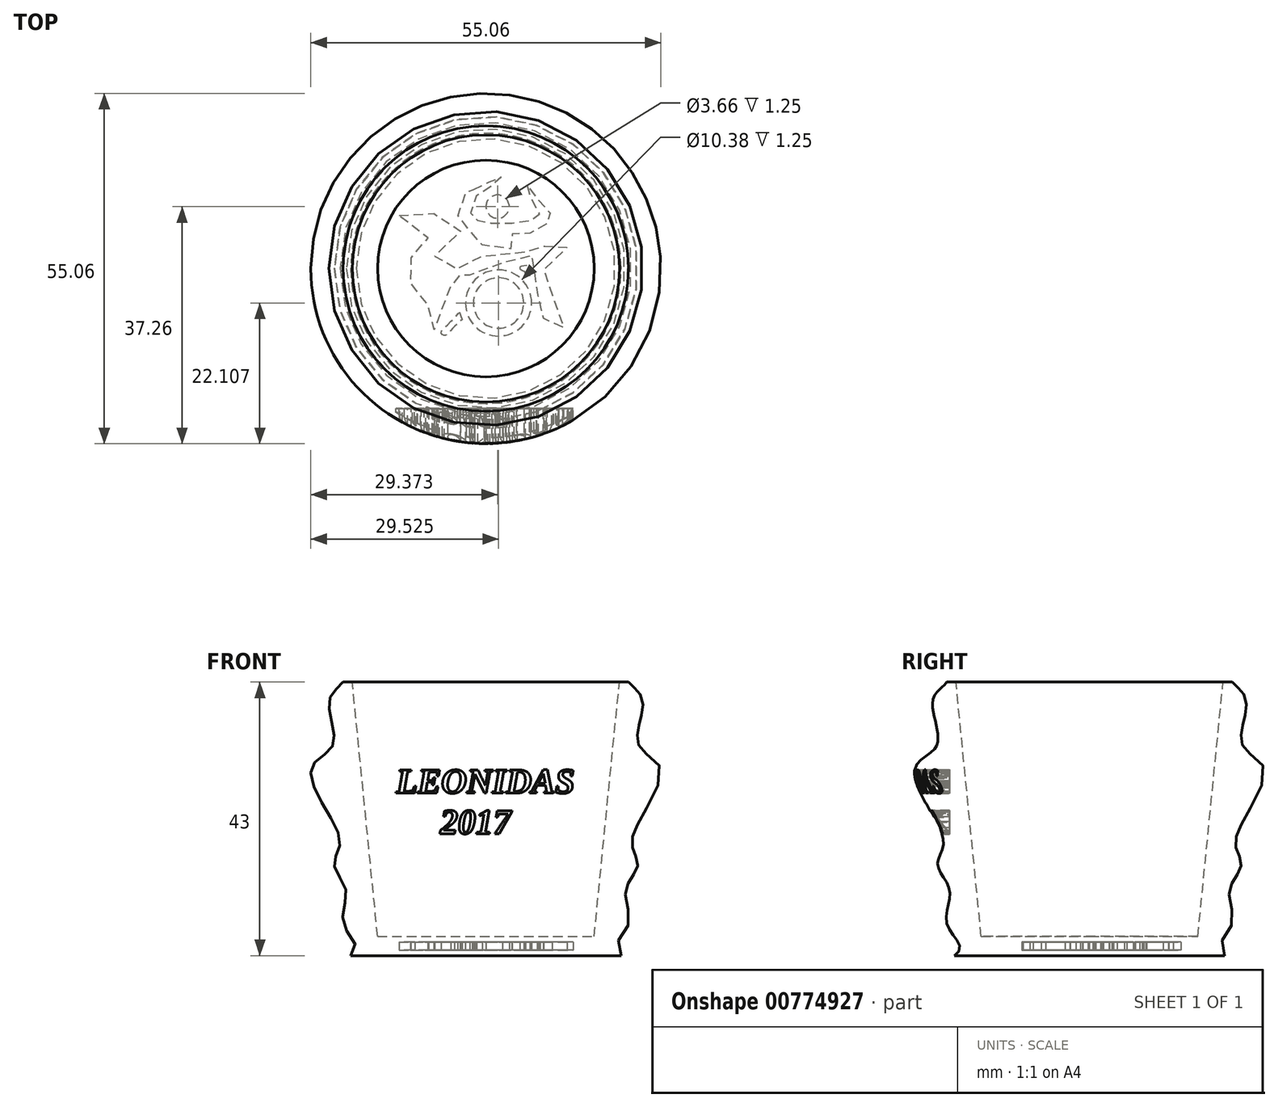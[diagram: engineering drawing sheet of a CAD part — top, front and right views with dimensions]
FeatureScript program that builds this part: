
annotation { "Feature Type Name" : "Feature", "Feature Type Description" : "" }
export const myFeature = defineFeature(function(context is Context, id is Id, definition is map)
    precondition{}
    {
        {
            var Q0;
            Q0=qCreatedBy(makeId("Front.planeOp"),FACE);
            var sketch = newSketch(context, id + "F0", { "sketchPlane" : qUnion([Q0])});
            skLineSegment(sketch, "E0", {"start": v(22.45, 43) * mm, "end": v(21, 43) * mm});
            skLineSegment(sketch, "E1", {"start": v(21, 43) * mm, "end": v(17.03, 3) * mm});
            skLineSegment(sketch, "E2", {"start": v(17.03, 3) * mm, "end": v(0, 3) * mm});
            skLineSegment(sketch, "E3", {"start": v(15.16, 0) * mm, "end": v(0, 0) * mm});
            skLineSegment(sketch, "E4", {"start": v(0, 0) * mm, "end": v(0, 3) * mm});
            skLineSegment(sketch, "E5", {"start": v(15.16, 0) * mm, "end": v(21.26, 0) * mm});
            skFitSpline(sketch, "E6", {"points": [v(21.26, 0) * mm, v(22.3, 4.61) * mm, v(21.97, 10.14) * mm, v(23.88, 14.27) * mm, v(22.95, 17.55) * mm, v(25.87, 24.2) * mm, v(27.28, 29.9) * mm, v(24.26, 32.61) * mm, v(24.2, 36.65) * mm, v(24.41, 40.88) * mm, v(22.45, 43) * mm], "startDerivative": vector(-64.03, 39.45) * mm, "endDerivative": vector(-12.25, 23.77) * mm});
            skSolve(sketch);
        }
        {
            var Q0;
            Q0=qSketchRegion(id+"F0",true);
            var Q1;
            Q1=sQuery(id+"F0.wireOp",EDGE,"E4");
            revolve(context, id + "F1", {"surfaceOperationType" : NewSurfaceOperationType.NEW, "entities" : qUnion([Q0]), "axis" : qUnion([Q1]), "revolveType" : RevolveType.FULL});
        }
        {
            var Q0;
            Q0=qCreatedBy(makeId("Top.planeOp"),FACE);
            cPlane(context, id + "F2", {"entities" : qUnion([Q0]), "cplaneType" : CPlaneType.OFFSET, "offset" : 1.5 * mm, "width" : 150 * mm, "height" : 150 * mm});
        }
        {
            var Q0;
            Q0=qCreatedBy(id+"F2.planeOp",FACE);
            var sketch = newSketch(context, id + "F3", { "sketchPlane" : qUnion([Q0])});
            skFitSpline(sketch, "E7", {"points": [v(-13.66, 8.35) * mm, v(-12.15, 8.52) * mm, v(-10.61, 8.5) * mm, v(-9.42, 8.3) * mm, v(-9.1, 8.32) * mm, v(-9.04, 8.6) * mm, v(-8.61, 8.95) * mm, v(-8.2, 8.66) * mm, v(-8.13, 8.12) * mm, v(-8.1, 8.01) * mm, v(-7.15, 7.7) * mm, v(-6.07, 7.27) * mm, v(-5.15, 6.75) * mm, v(-3.96, 6.08) * mm, v(-3.83, 5.9) * mm, v(-4.16, 5.9) * mm, v(-6.38, 6.46) * mm, v(-7.96, 6.86) * mm, v(-8.05, 6.86) * mm, v(-8.07, 6.46) * mm, v(-8.07, 1.94) * mm, v(-8.02, 1.9) * mm, v(-5.5, 1.92) * mm, v(-5.06, 1.74) * mm, v(-5, 1.25) * mm, v(-5.33, 0.89) * mm, v(-5.49, 0.86) * mm, v(-5.48, 0) * mm, v(-5.33, -0.04) * mm, v(-1.8, -0.06) * mm, v(-1.68, -0.01) * mm, v(-1.68, 0.32) * mm, v(-1.7, 0.85) * mm, v(-1.78, 0.9) * mm, v(-2.1, 1.13) * mm, v(-2.07, 1.67) * mm, v(-1.53, 1.88) * mm, v(0.6, 1.9) * mm, v(3.43, 1.9) * mm, v(4.27, 1.87) * mm, v(4.51, 1.76) * mm, v(4.74, 1.8) * mm, v(5.28, 2.11) * mm, v(6.26, 2.68) * mm, v(7.72, 3.2) * mm, v(8.17, 3.34) * mm, v(8.12, 3.6) * mm, v(8.21, 4.06) * mm, v(8.57, 4.34) * mm, v(8.93, 4.2) * mm, v(9.08, 3.8) * mm, v(9.1, 3.5) * mm, v(9.25, 3.54) * mm, v(9.9, 3.7) * mm, v(11.26, 3.75) * mm, v(12.15, 3.77) * mm, v(12.97, 3.72) * mm, v(13.66, 3.7) * mm, v(13.66, 3.5) * mm, v(12.88, 3.32) * mm, v(11.78, 3.05) * mm, v(10.77, 2.8) * mm, v(10.15, 2.69) * mm, v(9.35, 2.48) * mm, v(9.08, 2.4) * mm, v(9.07, 2.13) * mm, v(9.09, -1.13) * mm, v(9.02, -5.98) * mm, v(9.12, -6.2) * mm, v(10.61, -7.63) * mm, v(12.01, -9.1) * mm, v(12.74, -9.9) * mm, v(12.74, -10.27) * mm, v(12.43, -10.43) * mm, v(12.17, -10.46) * mm, v(11.7, -10.05) * mm, v(9.34, -7.73) * mm, v(9.06, -7.6) * mm, v(9.12, -8.2) * mm, v(8.9, -8.78) * mm, v(8.32, -8.78) * mm, v(8.1, -8.05) * mm, v(8.13, -6.92) * mm, v(8.33, -5.31) * mm, v(8.22, -4.15) * mm, v(8.11, -3.63) * mm, v(8.1, -1.35) * mm, v(8.11, 0.64) * mm, v(8.13, 2.1) * mm, v(8.11, 2.2) * mm, v(7.38, 2.03) * mm, v(5.56, 1.55) * mm, v(4.7, 1.33) * mm, v(4.61, 1.19) * mm, v(4.48, 1) * mm, v(4.23, 0.92) * mm, v(4.14, 0.85) * mm, v(4.16, 0.64) * mm, v(4.15, 0.55) * mm, v(3.55, 0.78) * mm, v(1.83, 0.94) * mm, v(0.7, 0.8) * mm, v(-0.14, 0.59) * mm, v(-1.2, 0.08) * mm, v(-1.38, -0.08) * mm, v(-1.8, -0.42) * mm, v(-2.18, -0.65) * mm, v(-3.6, -2.3) * mm, v(-3.88, -3.14) * mm, v(-4.04, -3.83) * mm, v(-4.06, -2.77) * mm, v(-4.05, -1.84) * mm, v(-4.05, -1.14) * mm, v(-4.05, -1.1) * mm, v(-4.43, -1.1) * mm, v(-5.42, -1.09) * mm, v(-5.47, -1.18) * mm, v(-5.51, -1.68) * mm, v(-5.48, -2.1) * mm, v(-5.35, -2.12) * mm, v(-5.02, -2.33) * mm, v(-4.97, -2.74) * mm, v(-5.18, -2.98) * mm, v(-5.26, -3.03) * mm, v(-5.46, -3.04) * mm, v(-7.94, -3.01) * mm, v(-8.12, -3.07) * mm, v(-8.1, -3.52) * mm, v(-8.15, -7.66) * mm, v(-8.15, -9.17) * mm, v(-8.12, -10.17) * mm, v(-8.19, -10.33) * mm, v(-8.46, -10.52) * mm, v(-8.77, -10.5) * mm, v(-8.96, -10.3) * mm, v(-9.1, -10.03) * mm, v(-9.04, -8.29) * mm, v(-9.1, -5.76) * mm, v(-9.08, -3.88) * mm, v(-9.04, -3.2) * mm, v(-9.08, -3.04) * mm, v(-9.42, -3.07) * mm, v(-11.4, -3.03) * mm, v(-11.7, -2.9) * mm, v(-11.78, -2.55) * mm, v(-11.75, -2.29) * mm, v(-11.46, -2.15) * mm, v(-11.22, -2.02) * mm, v(-11.19, 0) * mm, v(-11.19, 0.63) * mm, v(-11.24, 0.89) * mm, v(-11.44, 0.93) * mm, v(-11.77, 1.16) * mm, v(-11.86, 1.5) * mm, v(-11.75, 1.69) * mm, v(-11.58, 1.83) * mm, v(-11.3, 1.9) * mm, v(-10.97, 1.93) * mm, v(-10.43, 1.92) * mm, v(-9.76, 1.91) * mm, v(-9.3, 1.9) * mm, v(-9.22, 1.9) * mm, v(-9.13, 1.9) * mm, v(-9.1, 2) * mm, v(-9.1, 5.64) * mm, v(-9.11, 6.43) * mm, v(-9.12, 7.02) * mm, v(-9.18, 7.15) * mm, v(-9.99, 7.33) * mm, v(-12.26, 7.85) * mm, v(-13.66, 8.35) * mm]});
            skFitSpline(sketch, "E8", {"points": [v(5.35, -0.07) * mm, v(5.6, -0.19) * mm, v(6.01, -0.5) * mm, v(6.41, -0.86) * mm, v(6.67, -1.13) * mm, v(6.92, -1.44) * mm, v(6.92, -1.35) * mm, v(6.91, -0.4) * mm, v(6.92, 0.34) * mm, v(6.9, 0.64) * mm, v(6.8, 0.6) * mm, v(6.23, 0.46) * mm, v(5.44, 0.29) * mm, v(5.36, 0.26) * mm, v(5.35, -0.07) * mm]});
            skFitSpline(sketch, "E9", {"points": [v(-4.1, -6.9) * mm, v(-4.03, -7.23) * mm, v(-3.87, -7.7) * mm, v(-3.72, -8) * mm, v(-3.98, -8.27) * mm, v(-4.83, -9.06) * mm, v(-5.58, -9.8) * mm, v(-6.24, -10.46) * mm, v(-6.6, -10.54) * mm, v(-6.92, -10.33) * mm, v(-7.02, -10.08) * mm, v(-6.92, -9.74) * mm, v(-6.6, -9.42) * mm, v(-5.37, -8.18) * mm, v(-4.59, -7.4) * mm, v(-4.1, -6.9) * mm]});
            skCircle(sketch, "E10", {"center": v(2, -5.42) * mm, "radius": 3.96 * mm});
            skCircle(sketch, "E11", {"center": v(2, -5.42) * mm, "radius": 5.2 * mm});
            skCircle(sketch, "E12", {"center": v(1.84, 9.73) * mm, "radius": 1.83 * mm});
            skFitSpline(sketch, "E13", {"points": [v(-1.95, 12.44) * mm, v(-1.18, 12.85) * mm, v(-0.4, 13.18) * mm, v(0.41, 13.53) * mm, v(0.86, 13.72) * mm, v(1.48, 13.96) * mm, v(1.87, 14.15) * mm, v(2.26, 14.3) * mm, v(2.41, 14.36) * mm, v(2.62, 14.22) * mm, v(2.57, 13.98) * mm, v(2.11, 13.66) * mm, v(1.13, 13.12) * mm, v(-1.1, 11.9) * mm, v(-1.4, 11.74) * mm, v(-1.47, 11.64) * mm, v(-1.46, 11.54) * mm, v(-1.57, 11.2) * mm, v(-2.08, 9.65) * mm, v(-2.27, 9.2) * mm, v(-2.4, 8.75) * mm, v(-2.52, 8.43) * mm, v(-2.52, 8.33) * mm, v(-2.27, 8.15) * mm, v(-1.8, 7.9) * mm, v(-1.38, 7.63) * mm, v(-1, 7.42) * mm, v(-0.7, 7.26) * mm, v(-0.57, 7.2) * mm, v(-0.35, 7.2) * mm, v(0.86, 7.15) * mm, v(1.6, 7.15) * mm, v(3.09, 7.15) * mm, v(4.84, 7.16) * mm, v(6.33, 7.18) * mm, v(6.44, 7.18) * mm, v(6.6, 7.27) * mm, v(7.52, 7.82) * mm, v(7.8, 7.97) * mm, v(8.11, 8.17) * mm, v(8.48, 8.38) * mm, v(8.54, 8.47) * mm, v(8.43, 8.61) * mm, v(7.96, 9.55) * mm, v(7.56, 10.3) * mm, v(6.72, 11.87) * mm, v(6.34, 12.6) * mm, v(6.28, 12.81) * mm, v(6.27, 13) * mm, v(6.35, 13.09) * mm, v(6.44, 13.13) * mm, v(6.56, 13.12) * mm, v(6.62, 13.07) * mm, v(6.73, 12.95) * mm, v(6.97, 12.59) * mm, v(8, 11.07) * mm, v(9.4, 8.9) * mm, v(9.44, 8.86) * mm, v(9.67, 8.88) * mm, v(9.97, 8.8) * mm, v(10.31, 8.48) * mm, v(10.44, 7.9) * mm, v(10.2, 7.45) * mm, v(9.81, 7.17) * mm, v(9.33, 6.9) * mm, v(7.35, 5.74) * mm, v(7.21, 5.65) * mm, v(7.01, 5.55) * mm, v(6.62, 5.51) * mm, v(5, 5.46) * mm, v(4.34, 5.46) * mm, v(4.17, 5.45) * mm, v(4.07, 5.35) * mm, v(4.08, 5.11) * mm, v(4.09, 3.35) * mm, v(4.06, 3.13) * mm, v(3.84, 3.1) * mm, v(-0.45, 3.1) * mm, v(-0.56, 3.1) * mm, v(-0.56, 5.1) * mm, v(-0.56, 5.18) * mm, v(-0.68, 5.25) * mm, v(-4, 7.24) * mm, v(-4.19, 7.38) * mm, v(-4.3, 7.59) * mm, v(-4.4, 7.92) * mm, v(-4.4, 8.22) * mm, v(-4.34, 8.4) * mm, v(-3.84, 9.88) * mm, v(-3.14, 11.9) * mm, v(-3.02, 12.14) * mm, v(-2.88, 12.29) * mm, v(-2.73, 12.4) * mm, v(-2.46, 12.48) * mm, v(-2.23, 12.47) * mm, v(-2.1, 12.45) * mm, v(-1.95, 12.44) * mm]});
            skSolve(sketch);
        }
        {
            var Q0;
            Q0 = qSketchRegion(id + "F3", true);
            extrude(context, id + "F4", {"entities" : qUnion([Q0]), "operationType" : NewBodyOperationType.REMOVE, "endBound" : BoundingType.SYMMETRIC, "depth" : 1.25 * mm, "offsetDistance" : 25 * mm});
        }
        {
            var Q0;
            Q0=qCreatedBy(makeId("Front.planeOp"),FACE);
            cPlane(context, id + "F5", {"entities" : qUnion([Q0]), "cplaneType" : CPlaneType.OFFSET, "offset" : 22 * mm, "width" : 150 * mm, "height" : 150 * mm});
        }
        {
            var Q0;
            Q0=qCreatedBy(id+"F5.planeOp",FACE);
            var sketch = newSketch(context, id + "F6", { "sketchPlane" : qUnion([Q0])});
            skText(sketch, "E14", { "text": "LEONIDAS\n     2017", "fontName": "Tinos-BoldItalic.ttf"});
            const initialGuessF6  = {"E14": [-0.01412, 0.02555, 1, 0, 0.004]};
            skSetInitialGuess(sketch, initialGuessF6);
            skSolve(sketch);
        }
        {
            var Q0;
            Q0 = qSketchRegion(id + "F6", true);
            extrude(context, id + "F7", {"entities" : qUnion([Q0]), "operationType" : NewBodyOperationType.REMOVE, "depth" : 25 * mm, "offsetDistance" : 25 * mm});
        }
    });
